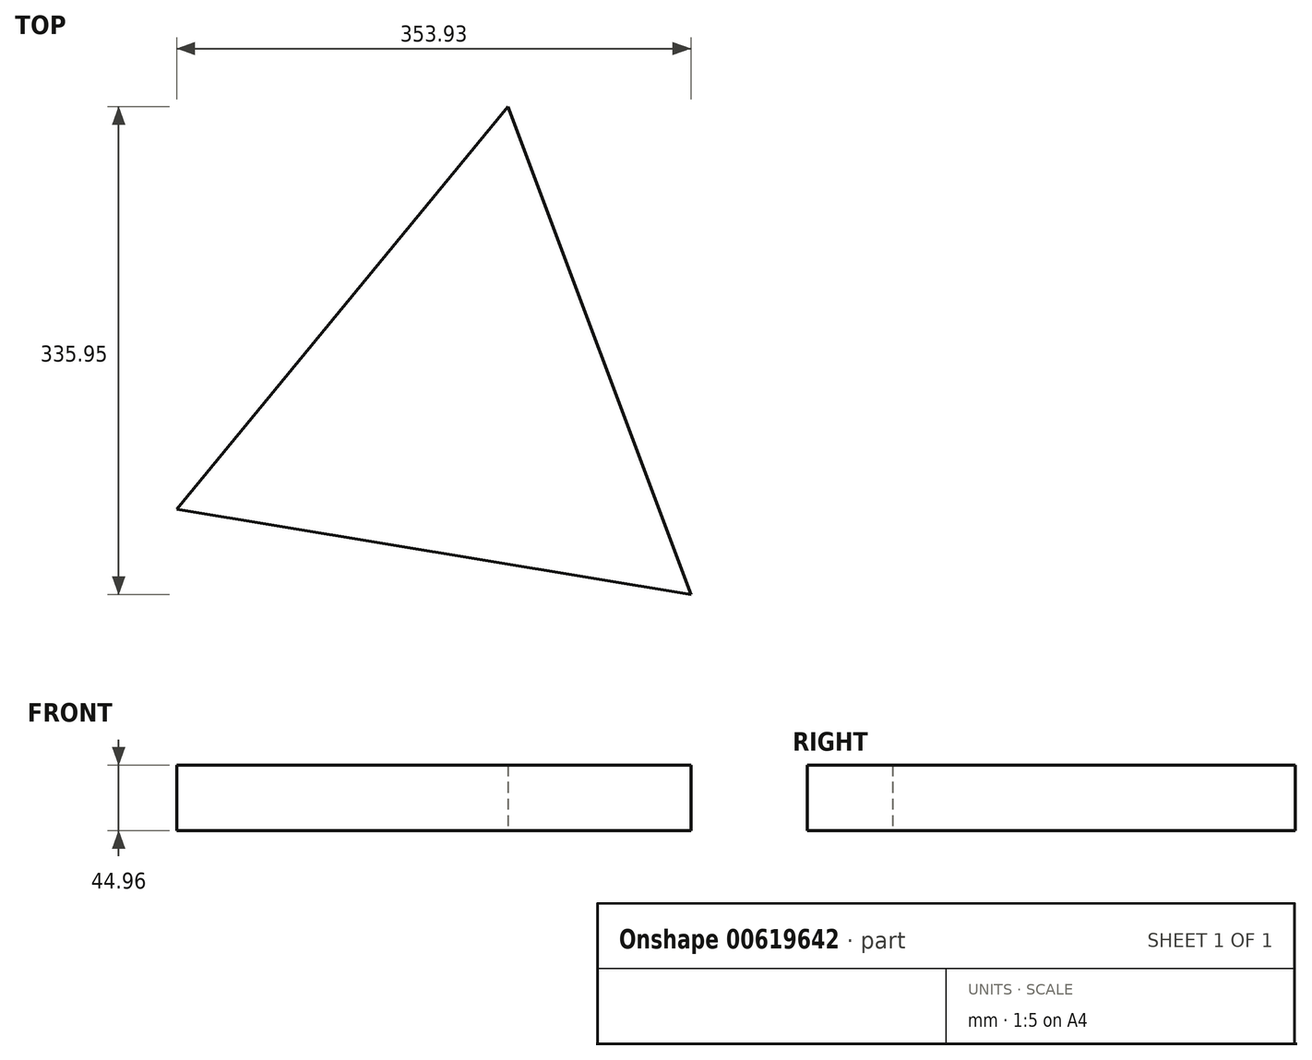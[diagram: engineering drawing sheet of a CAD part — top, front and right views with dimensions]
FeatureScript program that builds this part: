
annotation { "Feature Type Name" : "Feature", "Feature Type Description" : "" }
export const myFeature = defineFeature(function(context is Context, id is Id, definition is map)
    precondition{}
    {
        {
            var Q0;
            Q0=qCreatedBy(makeId("Top.planeOp"),FACE);
            var sketch = newSketch(context, id + "F0", { "sketchPlane" : qUnion([Q0])});
            skCircle(sketch, "E0.cCircle", {"center": v(0, 0) * mm, "radius": 103.58 * mm, "construction": true});
            skLineSegment(sketch, "E0.0", {"start": v(-193.96, -72.74) * mm, "end": v(34, 204.34) * mm});
            skLineSegment(sketch, "E0.1", {"start": v(34, 204.34) * mm, "end": v(159.97, -131.6) * mm});
            skLineSegment(sketch, "E0.2", {"start": v(159.97, -131.6) * mm, "end": v(-193.96, -72.74) * mm});
            skPoint(sketch, "E0.0.midPoint", {"position": v(-79.99, 65.8) * mm});
            skSolve(sketch);
        }
        {
            var Q0;
            Q0=makeQuery(id+"F0.imprint","IMPRINT",FACE,{"disambiguationData":[TD([[makeQuery(id+"F0.imprint","IMPRINT",EDGE,{"derivedFrom":sQuery(id+"F0.wireOp",EDGE,"E0.0")}),-1.0]])]});
            extrude(context, id + "F1", {"entities" : qUnion([Q0]), "depth" : 44.96 * mm, "offsetDistance" : 25.4 * mm});
        }
    });
